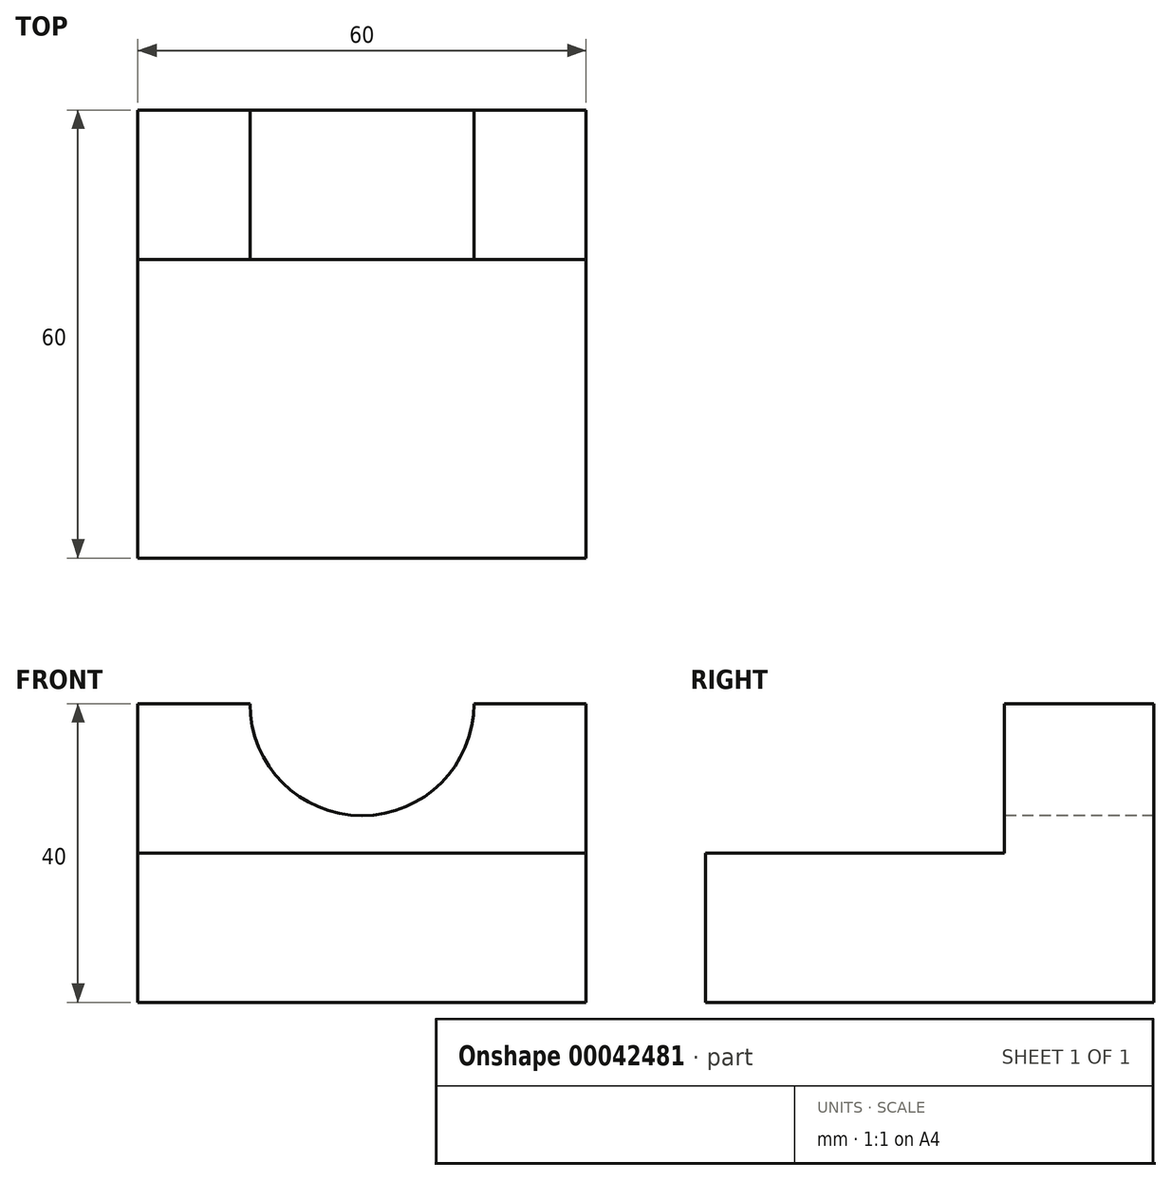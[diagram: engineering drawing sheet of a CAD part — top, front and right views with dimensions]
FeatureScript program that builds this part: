
annotation { "Feature Type Name" : "Feature", "Feature Type Description" : "" }
export const myFeature = defineFeature(function(context is Context, id is Id, definition is map)
    precondition{}
    {
        {
            var Q0;
            Q0=qCreatedBy(makeId("Top.planeOp"),FACE);
            var sketch = newSketch(context, id + "F0", { "sketchPlane" : qUnion([Q0])});
            skLineSegment(sketch, "E0.bottom", {"start": v(0, 0) * mm, "end": v(60, 0) * mm});
            skLineSegment(sketch, "E0.top", {"start": v(0, 60) * mm, "end": v(60, 60) * mm});
            skLineSegment(sketch, "E0.left", {"start": v(0, 0) * mm, "end": v(0, 60) * mm});
            skLineSegment(sketch, "E0.right", {"start": v(60, 0) * mm, "end": v(60, 60) * mm});
            skSolve(sketch);
        }
        {
            var Q0;
            Q0=makeQuery(id+"F0.imprint","IMPRINT",FACE,{"disambiguationData":[TD([[makeQuery(id+"F0.imprint","IMPRINT",EDGE,{"derivedFrom":sQuery(id+"F0.wireOp",EDGE,"E0.bottom")}),1.0]])]});
            extrude(context, id + "F1", {"entities" : qUnion([Q0]), "oppositeDirection" : true, "depth" : 20 * mm});
        }
        {
            var Q0;
            Q0=makeQuery(id+"F1.opExtrude","CAP_FACE",FACE,{"disambiguationData":[OSD([sQuery(id+"F0.wireOp",EDGE,"E0.bottom"),sQuery(id+"F0.wireOp",EDGE,"E0.top"),sQuery(id+"F0.wireOp",EDGE,"E0.left"),sQuery(id+"F0.wireOp",EDGE,"E0.right")])],"isStart":false});
            var sketch = newSketch(context, id + "F2", { "sketchPlane" : qUnion([Q0])});
            skLineSegment(sketch, "E1", {"start": v(0, -40) * mm, "end": v(60, -40) * mm});
            skSolve(sketch);
        }
        {
            var Q0;
            {var subQ1=sQuery(id+"F2.wireOp",EDGE,"E1");Q0=makeQuery(id+"F2.imprint","IMPRINT",FACE,{"disambiguationData":[TD([[makeQuery(id+"F2.imprint","IMPRINT",EDGE,{"derivedFrom":subQ1}),-1.0]])]});}
            extrude(context, id + "F3", {"entities" : qUnion([Q0]), "operationType" : NewBodyOperationType.ADD, "oppositeDirection" : true, "depth" : 40 * mm});
        }
        {
            var Q0;
            Q0=makeQuery(id+"F3.opExtrude","SWEPT_FACE",FACE,{"disambiguationData":[OSD([sQuery(id+"F2.wireOp",EDGE,"E1")])]});
            var sketch = newSketch(context, id + "F4", { "sketchPlane" : qUnion([Q0])});
            skLineSegment(sketch, "E2", {"start": v(15, 0) * mm, "end": v(15, 20) * mm, "construction": true});
            skLineSegment(sketch, "E3", {"start": v(45, 20) * mm, "end": v(45, 0) * mm, "construction": true});
            skArc(sketch, "E4", {"start": v(15, 20) * mm, "mid": v(30, 5) * mm, "end": v(45, 20) * mm});
            skSolve(sketch);
        }
        {
            var Q0;
            {var subQ1=sQuery(id+"F4.wireOp",EDGE,"E4");Q0=makeQuery(id+"F4.imprint","IMPRINT",FACE,{"disambiguationData":[TD([[makeQuery(id+"F4.imprint","IMPRINT",EDGE,{"derivedFrom":subQ1}),1.0]])]});}
            extrude(context, id + "F5", {"entities" : qUnion([Q0]), "operationType" : NewBodyOperationType.REMOVE, "oppositeDirection" : true, "depth" : 25 * mm});
        }
    });
